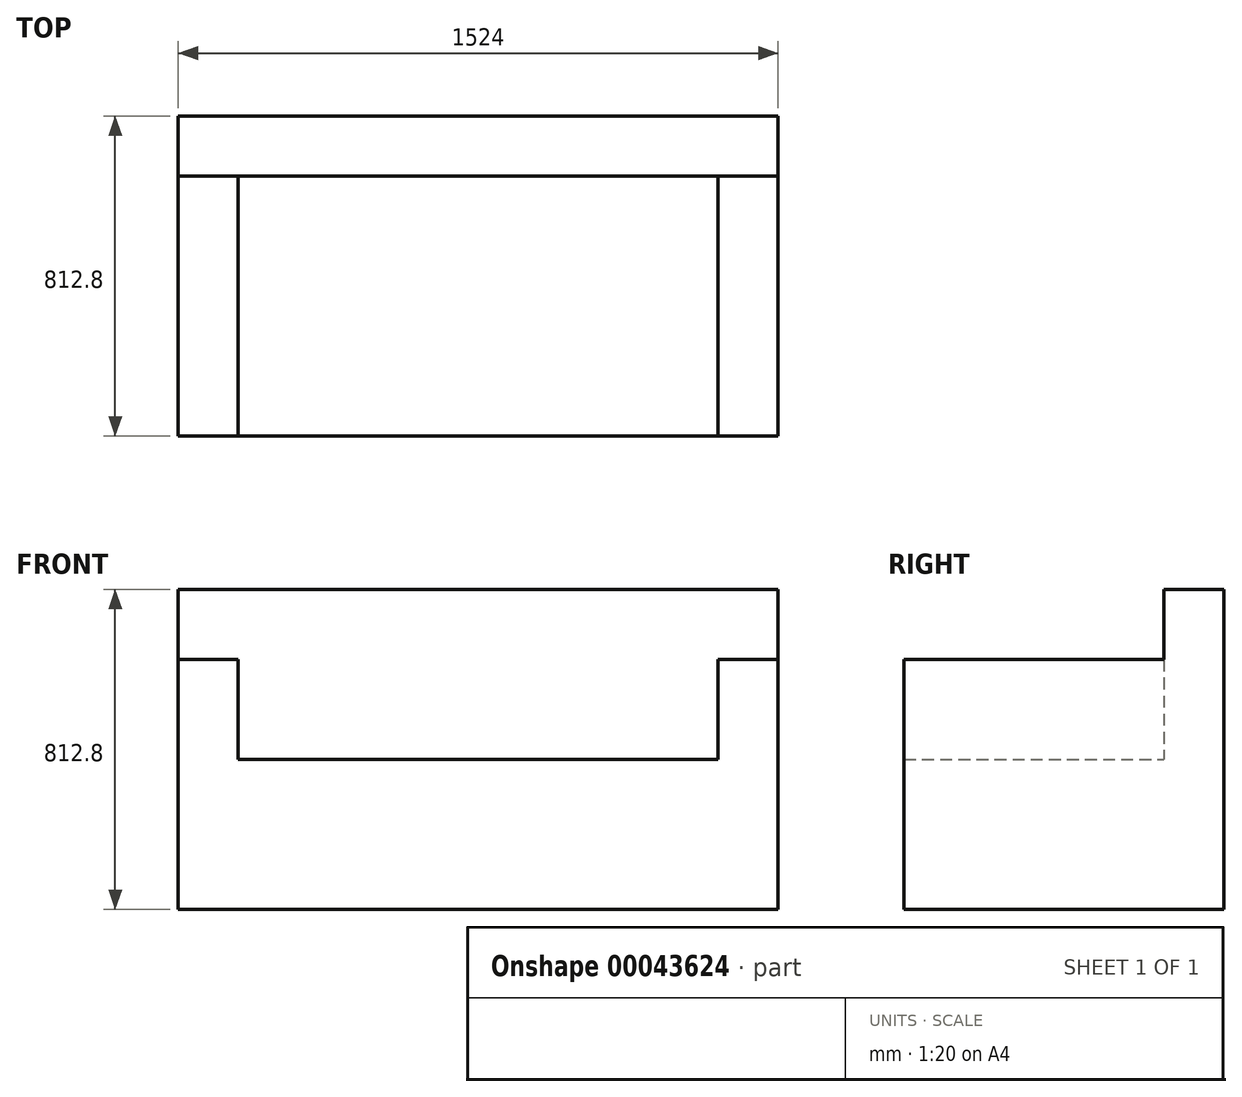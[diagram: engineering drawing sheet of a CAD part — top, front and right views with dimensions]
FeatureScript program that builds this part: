
annotation { "Feature Type Name" : "Feature", "Feature Type Description" : "" }
export const myFeature = defineFeature(function(context is Context, id is Id, definition is map)
    precondition{}
    {
        {
            var Q0;
            Q0=qCreatedBy(makeId("Top.planeOp"),FACE);
            var sketch = newSketch(context, id + "F0", { "sketchPlane" : qUnion([Q0])});
            skLineSegment(sketch, "E0.bottom", {"start": v(0, 0) * mm, "end": v(1524, 0) * mm});
            skLineSegment(sketch, "E0.top", {"start": v(0, -812.8) * mm, "end": v(1524, -812.8) * mm});
            skLineSegment(sketch, "E0.left", {"start": v(0, 0) * mm, "end": v(0, -812.8) * mm});
            skLineSegment(sketch, "E0.right", {"start": v(1524, 0) * mm, "end": v(1524, -812.8) * mm});
            skSolve(sketch);
        }
        {
            var Q0;
            Q0=qSketchRegion(id+"F0",true);
            extrude(context, id + "F1", {"entities" : qUnion([Q0]), "depth" : 381 * mm});
        }
        {
            var Q0;
            Q0=makeQuery(id+"F1.opExtrude","CAP_FACE",FACE,{"disambiguationData":[OSD([sQuery(id+"F0.wireOp",EDGE,"E0.bottom"),sQuery(id+"F0.wireOp",EDGE,"E0.top"),sQuery(id+"F0.wireOp",EDGE,"E0.left"),sQuery(id+"F0.wireOp",EDGE,"E0.right")])],"isStart":false});
            var sketch = newSketch(context, id + "F2", { "sketchPlane" : qUnion([Q0])});
            skLineSegment(sketch, "E1", {"start": v(0, -812.8) * mm, "end": v(0, 0) * mm});
            skLineSegment(sketch, "E2", {"start": v(0, 0) * mm, "end": v(1524, 0) * mm});
            skLineSegment(sketch, "E3", {"start": v(1524, 0) * mm, "end": v(1524, -812.8) * mm});
            skLineSegment(sketch, "E4", {"start": v(1524, -812.8) * mm, "end": v(1371.6, -812.8) * mm});
            skLineSegment(sketch, "E5", {"start": v(1371.6, -812.8) * mm, "end": v(1371.6, -152.4) * mm});
            skLineSegment(sketch, "E6", {"start": v(1371.6, -152.4) * mm, "end": v(152.4, -152.4) * mm});
            skLineSegment(sketch, "E7", {"start": v(152.4, -152.4) * mm, "end": v(152.4, -812.8) * mm});
            skLineSegment(sketch, "E8", {"start": v(152.4, -812.8) * mm, "end": v(0, -812.8) * mm});
            skSolve(sketch);
        }
        {
            var Q0;
            Q0=qSketchRegion(id+"F2",true);
            extrude(context, id + "F3", {"entities" : qUnion([Q0]), "operationType" : NewBodyOperationType.ADD, "depth" : 254 * mm});
        }
        {
            var Q0;
            Q0=makeQuery(id+"F3.opExtrude","CAP_FACE",FACE,{"disambiguationData":[OSD([sQuery(id+"F2.wireOp",EDGE,"E1"),sQuery(id+"F2.wireOp",EDGE,"E2"),sQuery(id+"F2.wireOp",EDGE,"E3"),sQuery(id+"F2.wireOp",EDGE,"E4"),sQuery(id+"F2.wireOp",EDGE,"E5"),sQuery(id+"F2.wireOp",EDGE,"E6"),sQuery(id+"F2.wireOp",EDGE,"E7"),sQuery(id+"F2.wireOp",EDGE,"E8")])],"isStart":false});
            var sketch = newSketch(context, id + "F4", { "sketchPlane" : qUnion([Q0])});
            skLineSegment(sketch, "E9.bottom", {"start": v(0, 0) * mm, "end": v(1524, 0) * mm});
            skLineSegment(sketch, "E9.top", {"start": v(0, -152.4) * mm, "end": v(1524, -152.4) * mm});
            skLineSegment(sketch, "E9.left", {"start": v(0, 0) * mm, "end": v(0, -152.4) * mm});
            skLineSegment(sketch, "E9.right", {"start": v(1524, 0) * mm, "end": v(1524, -152.4) * mm});
            skSolve(sketch);
        }
        {
            var Q0;
            Q0=qSketchRegion(id+"F4",true);
            extrude(context, id + "F5", {"entities" : qUnion([Q0]), "operationType" : NewBodyOperationType.ADD, "depth" : 177.8 * mm});
        }
    });
